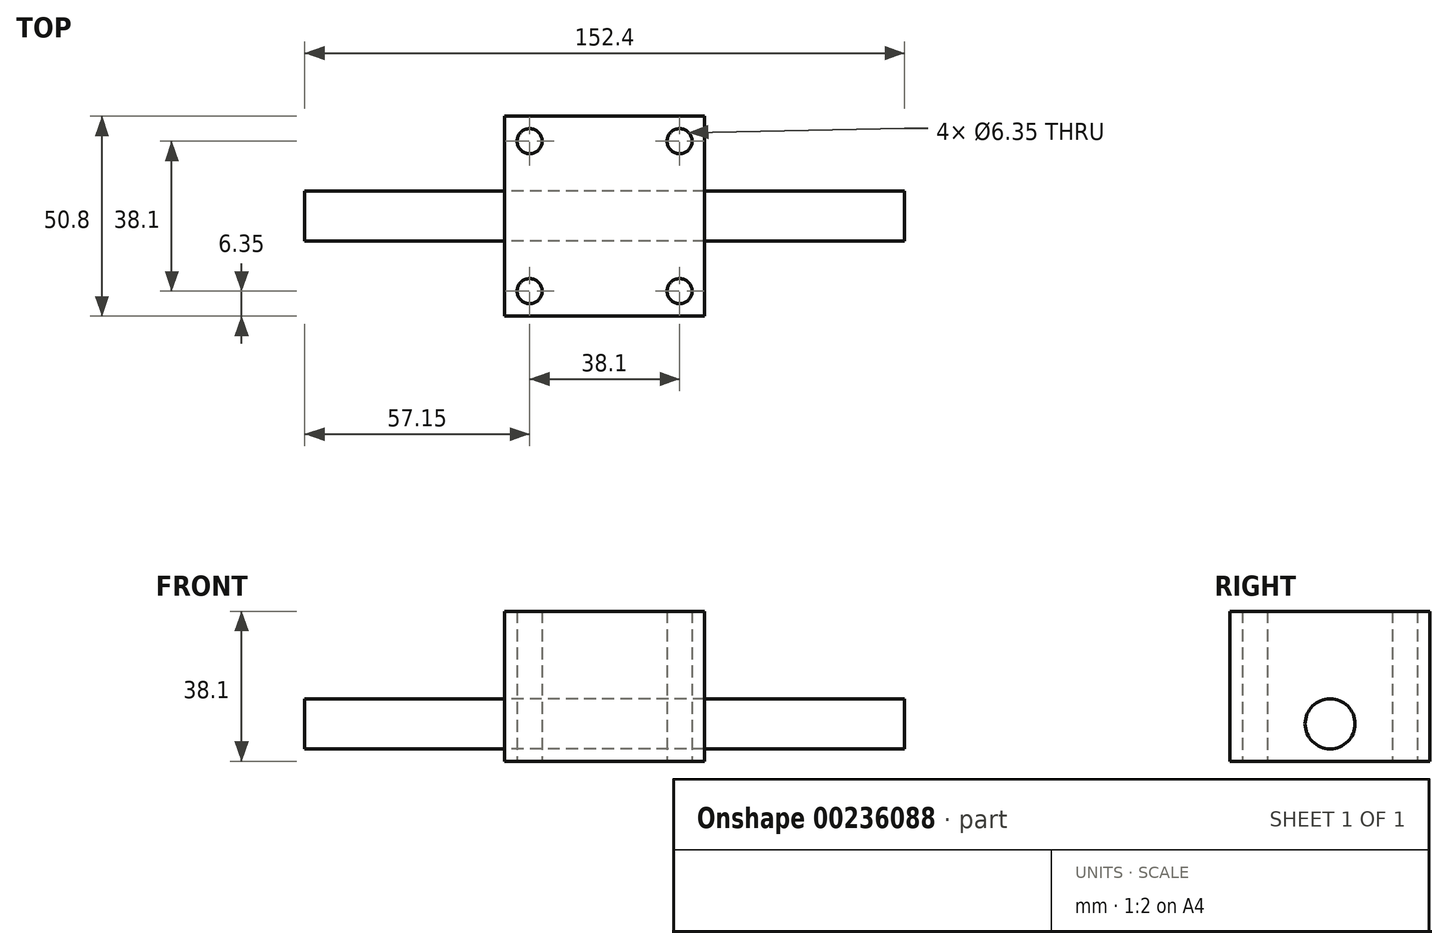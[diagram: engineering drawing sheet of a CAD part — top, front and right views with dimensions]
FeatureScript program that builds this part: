
annotation { "Feature Type Name" : "Feature", "Feature Type Description" : "" }
export const myFeature = defineFeature(function(context is Context, id is Id, definition is map)
    precondition{}
    {
        {
            var Q0;
            Q0=qCreatedBy(makeId("Top.planeOp"),FACE);
            var sketch = newSketch(context, id + "F0", { "sketchPlane" : qUnion([Q0])});
            skLineSegment(sketch, "E0.bottom", {"start": v(25.4, -25.4) * mm, "end": v(-25.4, -25.4) * mm});
            skLineSegment(sketch, "E0.top", {"start": v(25.4, 25.4) * mm, "end": v(-25.4, 25.4) * mm});
            skLineSegment(sketch, "E0.left", {"start": v(25.4, -25.4) * mm, "end": v(25.4, 25.4) * mm});
            skLineSegment(sketch, "E0.right", {"start": v(-25.4, -25.4) * mm, "end": v(-25.4, 25.4) * mm});
            skPoint(sketch, "E0.middle", {"position": v(0, 0) * mm});
            skCircle(sketch, "E1", {"center": v(-19.05, 19.05) * mm, "radius": 3.18 * mm});
            skCircle(sketch, "E2.MirrorC", {"center": v(19.05, 19.05) * mm, "radius": 3.18 * mm});
            skCircle(sketch, "E3.MirrorC", {"center": v(19.05, -19.05) * mm, "radius": 3.18 * mm});
            skCircle(sketch, "E4.MirrorC", {"center": v(-19.05, -19.05) * mm, "radius": 3.18 * mm});
            skSolve(sketch);
        }
        {
            var Q0;
            Q0=makeQuery(id+"F0.imprint","IMPRINT",FACE,{"disambiguationData":[TD([[makeQuery(id+"F0.imprint","IMPRINT",EDGE,{"derivedFrom":sQuery(id+"F0.wireOp",EDGE,"E0.bottom")}),-1.0]])]});
            extrude(context, id + "F1", {"entities" : qUnion([Q0]), "endBound" : BoundingType.SYMMETRIC, "depth" : 38.1 * mm});
        }
        {
            var Q0;
            Q0=qCreatedBy(makeId("Right.planeOp"),FACE);
            var sketch = newSketch(context, id + "F2", { "sketchPlane" : qUnion([Q0])});
            skCircle(sketch, "E5", {"center": v(0, -9.53) * mm, "radius": 6.35 * mm});
            skSolve(sketch);
        }
        {
            var Q0;
            Q0 = qSketchRegion(id + "F2", true);
            extrude(context, id + "F3", {"entities" : qUnion([Q0]), "endBound" : BoundingType.SYMMETRIC, "depth" : 152.4 * mm});
        }
    });
